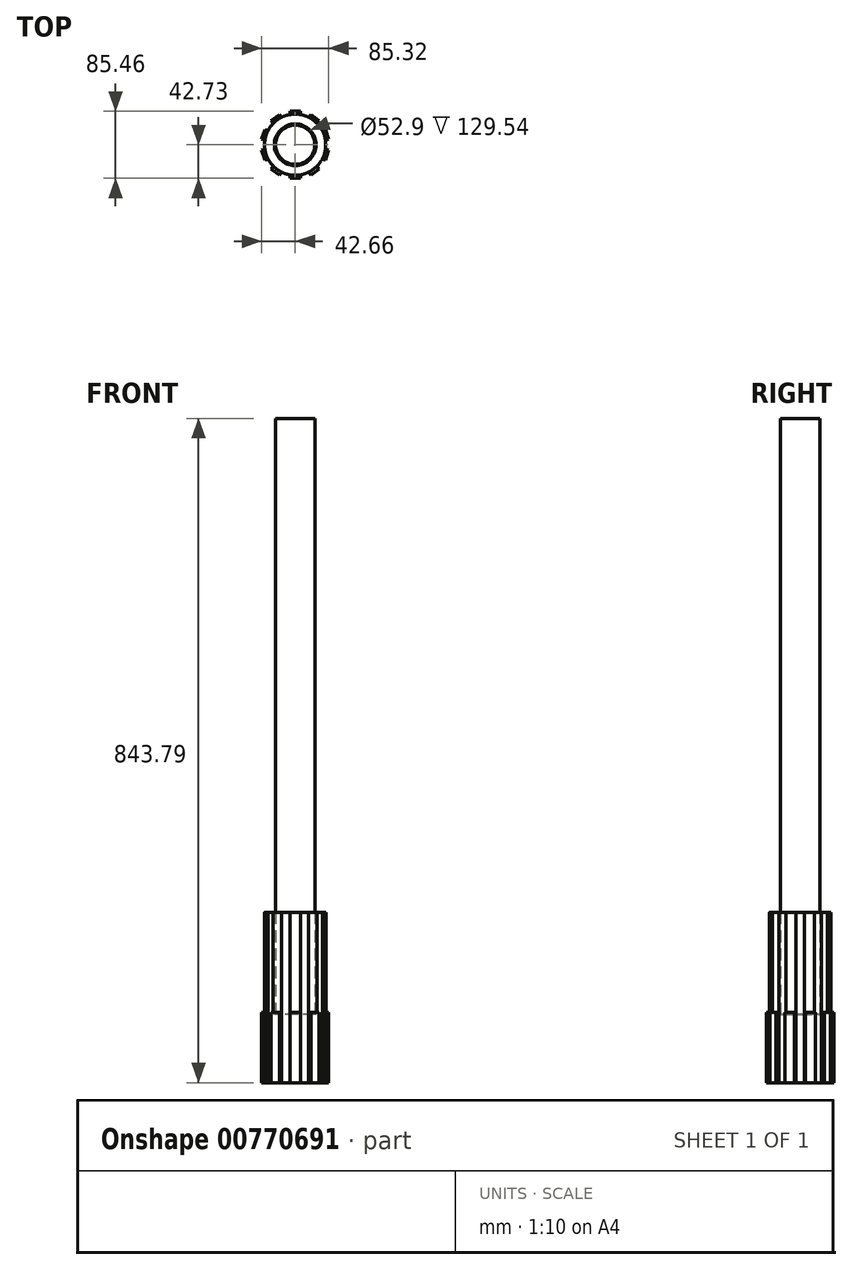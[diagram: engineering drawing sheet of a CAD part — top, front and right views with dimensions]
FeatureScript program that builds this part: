
annotation { "Feature Type Name" : "Feature", "Feature Type Description" : "" }
export const myFeature = defineFeature(function(context is Context, id is Id, definition is map)
    precondition{}
    {
        {
            var Q0;
            Q0=qCreatedBy(makeId("Top.planeOp"),FACE);
            var sketch = newSketch(context, id + "F0", { "sketchPlane" : qUnion([Q0])});
            skCircle(sketch, "E0", {"center": v(0, 0) * mm, "radius": 38.87 * mm});
            skLineSegment(sketch, "E1.bottom", {"start": v(6.55, 35) * mm, "end": v(-6.55, 35) * mm});
            skLineSegment(sketch, "E1.top", {"start": v(6.55, 42.73) * mm, "end": v(-6.55, 42.73) * mm});
            skLineSegment(sketch, "E1.left", {"start": v(6.55, 35) * mm, "end": v(6.55, 42.73) * mm});
            skLineSegment(sketch, "E1.right", {"start": v(-6.55, 35) * mm, "end": v(-6.55, 42.73) * mm});
            skPoint(sketch, "E1.middle", {"position": v(0, 38.87) * mm});
            skLineSegment(sketch, "E2.1.0", {"start": v(-19.81, 38.42) * mm, "end": v(-30.42, 30.71) * mm});
            skLineSegment(sketch, "E2.1.1", {"start": v(-15.27, 32.17) * mm, "end": v(-25.88, 24.47) * mm});
            skLineSegment(sketch, "E2.1.2", {"start": v(-15.27, 32.17) * mm, "end": v(-19.81, 38.42) * mm});
            skLineSegment(sketch, "E2.1.3", {"start": v(-25.88, 24.47) * mm, "end": v(-30.42, 30.71) * mm});
            skLineSegment(sketch, "E2.2.0", {"start": v(-38.61, 19.43) * mm, "end": v(-42.66, 6.97) * mm});
            skLineSegment(sketch, "E2.2.1", {"start": v(-31.27, 17.05) * mm, "end": v(-35.32, 4.59) * mm});
            skLineSegment(sketch, "E2.2.2", {"start": v(-31.27, 17.05) * mm, "end": v(-38.61, 19.43) * mm});
            skLineSegment(sketch, "E2.2.3", {"start": v(-35.32, 4.59) * mm, "end": v(-42.66, 6.97) * mm});
            skLineSegment(sketch, "E2.3.0", {"start": v(-42.66, -6.97) * mm, "end": v(-38.61, -19.43) * mm});
            skLineSegment(sketch, "E2.3.1", {"start": v(-35.32, -4.59) * mm, "end": v(-31.27, -17.05) * mm});
            skLineSegment(sketch, "E2.3.2", {"start": v(-35.32, -4.59) * mm, "end": v(-42.66, -6.97) * mm});
            skLineSegment(sketch, "E2.3.3", {"start": v(-31.27, -17.05) * mm, "end": v(-38.61, -19.43) * mm});
            skLineSegment(sketch, "E2.4.0", {"start": v(-30.42, -30.71) * mm, "end": v(-19.81, -38.42) * mm});
            skLineSegment(sketch, "E2.4.1", {"start": v(-25.88, -24.47) * mm, "end": v(-15.27, -32.17) * mm});
            skLineSegment(sketch, "E2.4.2", {"start": v(-25.88, -24.47) * mm, "end": v(-30.42, -30.71) * mm});
            skLineSegment(sketch, "E2.4.3", {"start": v(-15.27, -32.17) * mm, "end": v(-19.81, -38.42) * mm});
            skLineSegment(sketch, "E2.5.0", {"start": v(-6.55, -42.73) * mm, "end": v(6.55, -42.73) * mm});
            skLineSegment(sketch, "E2.5.1", {"start": v(-6.55, -35) * mm, "end": v(6.55, -35) * mm});
            skLineSegment(sketch, "E2.5.2", {"start": v(-6.55, -35) * mm, "end": v(-6.55, -42.73) * mm});
            skLineSegment(sketch, "E2.5.3", {"start": v(6.55, -35) * mm, "end": v(6.55, -42.73) * mm});
            skLineSegment(sketch, "E2.6.0", {"start": v(19.81, -38.42) * mm, "end": v(30.42, -30.71) * mm});
            skLineSegment(sketch, "E2.6.1", {"start": v(15.27, -32.17) * mm, "end": v(25.88, -24.47) * mm});
            skLineSegment(sketch, "E2.6.2", {"start": v(15.27, -32.17) * mm, "end": v(19.81, -38.42) * mm});
            skLineSegment(sketch, "E2.6.3", {"start": v(25.88, -24.47) * mm, "end": v(30.42, -30.71) * mm});
            skLineSegment(sketch, "E2.7.0", {"start": v(38.61, -19.43) * mm, "end": v(42.66, -6.97) * mm});
            skLineSegment(sketch, "E2.7.1", {"start": v(31.27, -17.05) * mm, "end": v(35.32, -4.59) * mm});
            skLineSegment(sketch, "E2.7.2", {"start": v(31.27, -17.05) * mm, "end": v(38.61, -19.43) * mm});
            skLineSegment(sketch, "E2.7.3", {"start": v(35.32, -4.59) * mm, "end": v(42.66, -6.97) * mm});
            skLineSegment(sketch, "E2.8.0", {"start": v(42.66, 6.97) * mm, "end": v(38.61, 19.43) * mm});
            skLineSegment(sketch, "E2.8.1", {"start": v(35.32, 4.59) * mm, "end": v(31.27, 17.05) * mm});
            skLineSegment(sketch, "E2.8.2", {"start": v(35.32, 4.59) * mm, "end": v(42.66, 6.97) * mm});
            skLineSegment(sketch, "E2.8.3", {"start": v(31.27, 17.05) * mm, "end": v(38.61, 19.43) * mm});
            skLineSegment(sketch, "E2.9.0", {"start": v(30.42, 30.71) * mm, "end": v(19.81, 38.42) * mm});
            skLineSegment(sketch, "E2.9.1", {"start": v(25.88, 24.47) * mm, "end": v(15.27, 32.17) * mm});
            skLineSegment(sketch, "E2.9.2", {"start": v(25.88, 24.47) * mm, "end": v(30.42, 30.71) * mm});
            skLineSegment(sketch, "E2.9.3", {"start": v(15.27, 32.17) * mm, "end": v(19.81, 38.42) * mm});
            skSolve(sketch);
        }
        {
            var Q0;
            {var subQ5=sQuery(id+"F0.wireOp",EDGE,"E2.1.1");Q0=makeQuery(id+"F0.imprint","IMPRINT",FACE,{"disambiguationData":[TD([[makeQuery(id+"F0.imprint","IMPRINT",EDGE,{"derivedFrom":subQ5}),-1.0]])]});}
            var Q1;
            {var subQ5=sQuery(id+"F0.wireOp",EDGE,"E2.1.0");Q1=makeQuery(id+"F0.imprint","IMPRINT",FACE,{"disambiguationData":[TD([[makeQuery(id+"F0.imprint","IMPRINT",EDGE,{"derivedFrom":subQ5}),1.0]])]});}
            var Q2;
            {var subQ5=sQuery(id+"F0.wireOp",EDGE,"E2.2.0");Q2=makeQuery(id+"F0.imprint","IMPRINT",FACE,{"disambiguationData":[TD([[makeQuery(id+"F0.imprint","IMPRINT",EDGE,{"derivedFrom":subQ5}),1.0]])]});}
            var Q3;
            {var subQ5=sQuery(id+"F0.wireOp",EDGE,"E2.2.1");Q3=makeQuery(id+"F0.imprint","IMPRINT",FACE,{"disambiguationData":[TD([[makeQuery(id+"F0.imprint","IMPRINT",EDGE,{"derivedFrom":subQ5}),-1.0]])]});}
            var Q4;
            {var subQ5=sQuery(id+"F0.wireOp",EDGE,"E2.3.0");Q4=makeQuery(id+"F0.imprint","IMPRINT",FACE,{"disambiguationData":[TD([[makeQuery(id+"F0.imprint","IMPRINT",EDGE,{"derivedFrom":subQ5}),1.0]])]});}
            var Q5;
            {var subQ5=sQuery(id+"F0.wireOp",EDGE,"E2.3.1");Q5=makeQuery(id+"F0.imprint","IMPRINT",FACE,{"disambiguationData":[TD([[makeQuery(id+"F0.imprint","IMPRINT",EDGE,{"derivedFrom":subQ5}),-1.0]])]});}
            var Q6;
            {var subQ5=sQuery(id+"F0.wireOp",EDGE,"E2.4.0");Q6=makeQuery(id+"F0.imprint","IMPRINT",FACE,{"disambiguationData":[TD([[makeQuery(id+"F0.imprint","IMPRINT",EDGE,{"derivedFrom":subQ5}),1.0]])]});}
            var Q7;
            {var subQ5=sQuery(id+"F0.wireOp",EDGE,"E2.4.1");Q7=makeQuery(id+"F0.imprint","IMPRINT",FACE,{"disambiguationData":[TD([[makeQuery(id+"F0.imprint","IMPRINT",EDGE,{"derivedFrom":subQ5}),-1.0]])]});}
            var Q8;
            {var subQ5=sQuery(id+"F0.wireOp",EDGE,"E2.5.0");Q8=makeQuery(id+"F0.imprint","IMPRINT",FACE,{"disambiguationData":[TD([[makeQuery(id+"F0.imprint","IMPRINT",EDGE,{"derivedFrom":subQ5}),1.0]])]});}
            var Q9;
            {var subQ5=sQuery(id+"F0.wireOp",EDGE,"E2.6.0");Q9=makeQuery(id+"F0.imprint","IMPRINT",FACE,{"disambiguationData":[TD([[makeQuery(id+"F0.imprint","IMPRINT",EDGE,{"derivedFrom":subQ5}),1.0]])]});}
            var Q10;
            {var subQ5=sQuery(id+"F0.wireOp",EDGE,"E2.6.1");Q10=makeQuery(id+"F0.imprint","IMPRINT",FACE,{"disambiguationData":[TD([[makeQuery(id+"F0.imprint","IMPRINT",EDGE,{"derivedFrom":subQ5}),-1.0]])]});}
            var Q11;
            {var subQ5=sQuery(id+"F0.wireOp",EDGE,"E2.7.1");Q11=makeQuery(id+"F0.imprint","IMPRINT",FACE,{"disambiguationData":[TD([[makeQuery(id+"F0.imprint","IMPRINT",EDGE,{"derivedFrom":subQ5}),-1.0]])]});}
            var Q12;
            {var subQ5=sQuery(id+"F0.wireOp",EDGE,"E2.7.0");Q12=makeQuery(id+"F0.imprint","IMPRINT",FACE,{"disambiguationData":[TD([[makeQuery(id+"F0.imprint","IMPRINT",EDGE,{"derivedFrom":subQ5}),1.0]])]});}
            var Q13;
            {var subQ5=sQuery(id+"F0.wireOp",EDGE,"E2.8.1");Q13=makeQuery(id+"F0.imprint","IMPRINT",FACE,{"disambiguationData":[TD([[makeQuery(id+"F0.imprint","IMPRINT",EDGE,{"derivedFrom":subQ5}),-1.0]])]});}
            var Q14;
            {var subQ5=sQuery(id+"F0.wireOp",EDGE,"E2.8.0");Q14=makeQuery(id+"F0.imprint","IMPRINT",FACE,{"disambiguationData":[TD([[makeQuery(id+"F0.imprint","IMPRINT",EDGE,{"derivedFrom":subQ5}),1.0]])]});}
            var Q15;
            {var subQ5=sQuery(id+"F0.wireOp",EDGE,"E2.9.1");Q15=makeQuery(id+"F0.imprint","IMPRINT",FACE,{"disambiguationData":[TD([[makeQuery(id+"F0.imprint","IMPRINT",EDGE,{"derivedFrom":subQ5}),-1.0]])]});}
            var Q16;
            {var subQ5=sQuery(id+"F0.wireOp",EDGE,"E2.9.0");Q16=makeQuery(id+"F0.imprint","IMPRINT",FACE,{"disambiguationData":[TD([[makeQuery(id+"F0.imprint","IMPRINT",EDGE,{"derivedFrom":subQ5}),1.0]])]});}
            var Q17;
            {var subQ5=sQuery(id+"F0.wireOp",EDGE,"E1.bottom");Q17=makeQuery(id+"F0.imprint","IMPRINT",FACE,{"disambiguationData":[TD([[makeQuery(id+"F0.imprint","IMPRINT",EDGE,{"derivedFrom":subQ5}),-1.0]])]});}
            var Q18;
            {var subQ5=sQuery(id+"F0.wireOp",EDGE,"E1.top");Q18=makeQuery(id+"F0.imprint","IMPRINT",FACE,{"disambiguationData":[TD([[makeQuery(id+"F0.imprint","IMPRINT",EDGE,{"derivedFrom":subQ5}),1.0]])]});}
            var Q19;
            {var subQ5=sQuery(id+"F0.wireOp",EDGE,"E2.5.1");Q19=makeQuery(id+"F0.imprint","IMPRINT",FACE,{"disambiguationData":[TD([[makeQuery(id+"F0.imprint","IMPRINT",EDGE,{"derivedFrom":subQ5}),-1.0]])]});}
            var Q20;
            {var subQ4=sQuery(id+"F0.wireOp",EDGE,"E1.bottom");Q20=makeQuery(id+"F0.imprint","IMPRINT",FACE,{"disambiguationData":[TD([[makeQuery(id+"F0.imprint","IMPRINT",EDGE,{"derivedFrom":subQ4}),1.0]])]});}
            extrude(context, id + "F1", {"entities" : qUnion([Q0, Q1, Q2, Q3, Q4, Q5, Q6, Q7, Q8, Q9, Q10, Q11, Q12, Q13, Q14, Q15, Q16, Q17, Q18, Q19, Q20]), "depth" : 89.4 * mm, "offsetDistance" : 25.4 * mm});
        }
        {
            var Q0;
            Q0=makeQuery(id+"F1.opExtrude","CAP_FACE",FACE,{"disambiguationData":[OSD([sQuery(id+"F0.wireOp",EDGE,"E0"),sQuery(id+"F0.wireOp",EDGE,"E1.top"),sQuery(id+"F0.wireOp",EDGE,"E1.left"),sQuery(id+"F0.wireOp",EDGE,"E1.right"),sQuery(id+"F0.wireOp",EDGE,"E2.1.0"),sQuery(id+"F0.wireOp",EDGE,"E2.1.2"),sQuery(id+"F0.wireOp",EDGE,"E2.1.3"),sQuery(id+"F0.wireOp",EDGE,"E2.2.0"),sQuery(id+"F0.wireOp",EDGE,"E2.2.2"),sQuery(id+"F0.wireOp",EDGE,"E2.2.3"),sQuery(id+"F0.wireOp",EDGE,"E2.3.0"),sQuery(id+"F0.wireOp",EDGE,"E2.3.2"),sQuery(id+"F0.wireOp",EDGE,"E2.3.3"),sQuery(id+"F0.wireOp",EDGE,"E2.4.0"),sQuery(id+"F0.wireOp",EDGE,"E2.4.2"),sQuery(id+"F0.wireOp",EDGE,"E2.4.3"),sQuery(id+"F0.wireOp",EDGE,"E2.5.0"),sQuery(id+"F0.wireOp",EDGE,"E2.5.2"),sQuery(id+"F0.wireOp",EDGE,"E2.5.3"),sQuery(id+"F0.wireOp",EDGE,"E2.6.0"),sQuery(id+"F0.wireOp",EDGE,"E2.6.2"),sQuery(id+"F0.wireOp",EDGE,"E2.6.3"),sQuery(id+"F0.wireOp",EDGE,"E2.7.0"),sQuery(id+"F0.wireOp",EDGE,"E2.7.2"),sQuery(id+"F0.wireOp",EDGE,"E2.7.3"),sQuery(id+"F0.wireOp",EDGE,"E2.8.0"),sQuery(id+"F0.wireOp",EDGE,"E2.8.2"),sQuery(id+"F0.wireOp",EDGE,"E2.8.3"),sQuery(id+"F0.wireOp",EDGE,"E2.9.0"),sQuery(id+"F0.wireOp",EDGE,"E2.9.2"),sQuery(id+"F0.wireOp",EDGE,"E2.9.3")])],"isStart":false});
            var sketch = newSketch(context, id + "F2", { "sketchPlane" : qUnion([Q0])});
            skCircle(sketch, "E3", {"center": v(0, 0) * mm, "radius": 38.88 * mm});
            skSolve(sketch);
        }
        {
            var Q0;
            {var subQ1=sQuery(id+"F0.wireOp",EDGE,"E0");var subQ4=sQuery(id+"F0.wireOp",EDGE,"E2.8.3");var subQ7=makeQuery(id+"F1.opExtrude","CAP_EDGE",EDGE,{"disambiguationData":[OSD([subQ1]),TDD([makeQuery(id+"F0.imprint","IMPRINT",EDGE,{"disambiguationData":[TD([[makeQuery(id+"F0.imprint","INTERSECT",VERTEX,{"derivedFrom":[subQ1,subQ4]}),-1.0]])],"derivedFrom":subQ1})])],"isStart":false});Q0=makeQuery(id+"F2.imprint","IMPRINT",FACE,{"disambiguationData":[TD([[makeQuery(id+"F2.imprint","IMPRINT",EDGE,{"derivedFrom":subQ7}),1.0]])]});}
            extrude(context, id + "F3", {"entities" : qUnion([Q0]), "operationType" : NewBodyOperationType.ADD, "depth" : 127 * mm, "offsetDistance" : 25.4 * mm});
        }
        {
            var Q0;
            Q0=makeQuery(id+"F3.opExtrude","CAP_FACE",FACE,{"disambiguationData":[OSD([sQuery(id+"F0.wireOp",EDGE,"E0"),sQuery(id+"F0.wireOp",EDGE,"E1.left"),sQuery(id+"F0.wireOp",EDGE,"E1.right"),sQuery(id+"F0.wireOp",EDGE,"E2.1.2"),sQuery(id+"F0.wireOp",EDGE,"E2.1.3"),sQuery(id+"F0.wireOp",EDGE,"E2.2.2"),sQuery(id+"F0.wireOp",EDGE,"E2.2.3"),sQuery(id+"F0.wireOp",EDGE,"E2.3.2"),sQuery(id+"F0.wireOp",EDGE,"E2.3.3"),sQuery(id+"F0.wireOp",EDGE,"E2.4.2"),sQuery(id+"F0.wireOp",EDGE,"E2.4.3"),sQuery(id+"F0.wireOp",EDGE,"E2.5.2"),sQuery(id+"F0.wireOp",EDGE,"E2.5.3"),sQuery(id+"F0.wireOp",EDGE,"E2.6.2"),sQuery(id+"F0.wireOp",EDGE,"E2.6.3"),sQuery(id+"F0.wireOp",EDGE,"E2.7.2"),sQuery(id+"F0.wireOp",EDGE,"E2.7.3"),sQuery(id+"F0.wireOp",EDGE,"E2.8.2"),sQuery(id+"F0.wireOp",EDGE,"E2.8.3"),sQuery(id+"F0.wireOp",EDGE,"E2.9.2"),sQuery(id+"F0.wireOp",EDGE,"E2.9.3"),sQuery(id+"F2.wireOp",EDGE,"E3")])],"isStart":false});
            var sketch = newSketch(context, id + "F4", { "sketchPlane" : qUnion([Q0])});
            skCircle(sketch, "E4", {"center": v(0, 0) * mm, "radius": 26.45 * mm});
            skSolve(sketch);
        }
        {
            var Q0;
            Q0=makeQuery(id+"F4.imprint","IMPRINT",FACE,{"disambiguationData":[TD([[makeQuery(id+"F4.imprint","IMPRINT",EDGE,{"derivedFrom":sQuery(id+"F4.wireOp",EDGE,"E4")}),1.0]])]});
            extrude(context, id + "F5", {"entities" : qUnion([Q0]), "operationType" : NewBodyOperationType.REMOVE, "oppositeDirection" : true, "depth" : 129.54 * mm, "offsetDistance" : 25.4 * mm});
        }
        {
            var Q0;
            Q0=makeQuery(id+"F5.boolean.opBoolean","COPY",FACE,{"derivedFrom":makeQuery(id+"F5.opExtrude","CAP_FACE",FACE,{"disambiguationData":[OSD([sQuery(id+"F4.wireOp",EDGE,"E4")])],"isStart":false})});
            var sketch = newSketch(context, id + "F6", { "sketchPlane" : qUnion([Q0])});
            skCircle(sketch, "E5", {"center": v(0, 0) * mm, "radius": 24.91 * mm});
            skSolve(sketch);
        }
        {
            var Q0;
            Q0=makeQuery(id+"F6.imprint","IMPRINT",FACE,{"disambiguationData":[TD([[makeQuery(id+"F6.imprint","IMPRINT",EDGE,{"derivedFrom":sQuery(id+"F6.wireOp",EDGE,"E5")}),1.0]])]});
            extrude(context, id + "F7", {"entities" : qUnion([Q0]), "operationType" : NewBodyOperationType.ADD, "depth" : 756.92 * mm, "offsetDistance" : 25.4 * mm});
        }
    });
